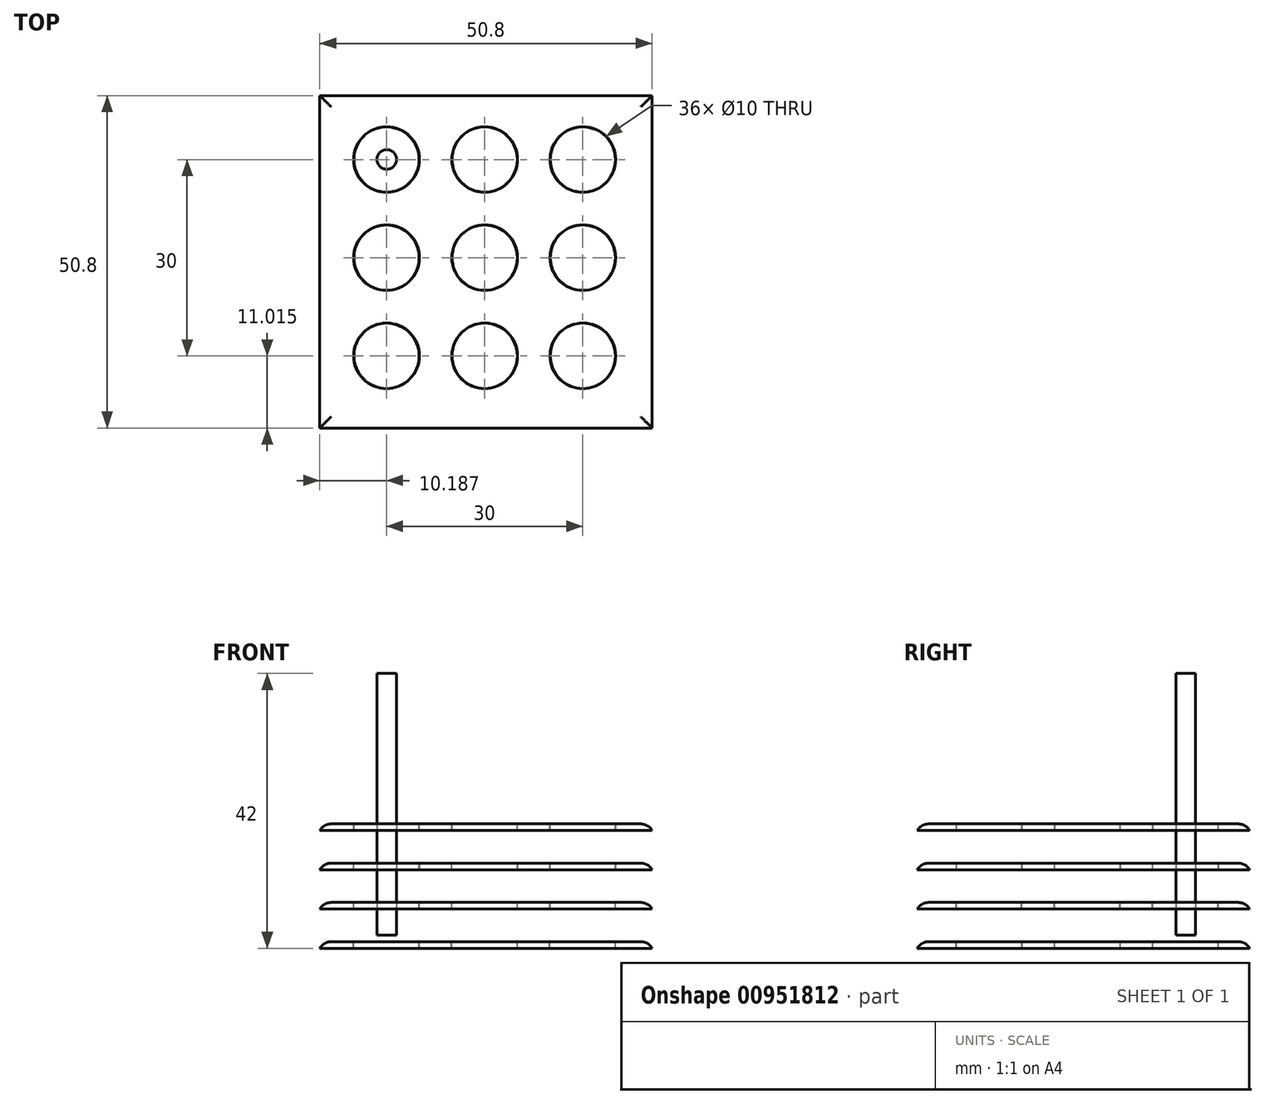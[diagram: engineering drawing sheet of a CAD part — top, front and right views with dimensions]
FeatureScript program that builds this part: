
annotation { "Feature Type Name" : "Feature", "Feature Type Description" : "" }
export const myFeature = defineFeature(function(context is Context, id is Id, definition is map)
    precondition{}
    {
        {
            var Q0;
            Q0=qCreatedBy(makeId("Top.planeOp"),FACE);
            var sketch = newSketch(context, id + "F0", { "sketchPlane" : qUnion([Q0])});
            skLineSegment(sketch, "E0.bottom", {"start": v(-21.15, 0) * mm, "end": v(29.65, 0) * mm});
            skLineSegment(sketch, "E0.top", {"start": v(-21.15, 50.8) * mm, "end": v(29.65, 50.8) * mm});
            skLineSegment(sketch, "E0.left", {"start": v(-21.15, 0) * mm, "end": v(-21.15, 50.8) * mm});
            skLineSegment(sketch, "E0.right", {"start": v(29.65, 0) * mm, "end": v(29.65, 50.8) * mm});
            skSolve(sketch);
        }
        {
            var Q0;
            Q0=makeQuery(id+"F0.imprint","IMPRINT",FACE,{"disambiguationData":[TD([[makeQuery(id+"F0.imprint","IMPRINT",EDGE,{"derivedFrom":sQuery(id+"F0.wireOp",EDGE,"E0.bottom")}),1.0]])]});
            extrude(context, id + "F1", {"entities" : qUnion([Q0]), "depth" : 1 * mm, "offsetDistance" : 25.4 * mm});
        }
        {
            var Q0;
            Q0=makeQuery(id+"F1.opExtrude","CAP_EDGE",EDGE,{"disambiguationData":[OSD([sQuery(id+"F0.wireOp",EDGE,"E0.bottom")])],"isStart":false});
            var Q1;
            Q1=makeQuery(id+"F1.opExtrude","CAP_EDGE",EDGE,{"disambiguationData":[OSD([sQuery(id+"F0.wireOp",EDGE,"E0.right")])],"isStart":false});
            var Q2;
            Q2=makeQuery(id+"F1.opExtrude","CAP_EDGE",EDGE,{"disambiguationData":[OSD([sQuery(id+"F0.wireOp",EDGE,"E0.top")])],"isStart":false});
            var Q3;
            Q3=makeQuery(id+"F1.opExtrude","CAP_EDGE",EDGE,{"disambiguationData":[OSD([sQuery(id+"F0.wireOp",EDGE,"E0.left")])],"isStart":false});
            fillet(context, id + "F2", {"entities" : qUnion([Q0, Q1, Q2, Q3]), "radius" : 2 * mm, "tangentPropagation" : true, "allowEdgeOverflow" : false});
        }
        {
            var Q0;
            Q0=makeQuery(id+"F1.opExtrude","CAP_FACE",FACE,{"disambiguationData":[OSD([sQuery(id+"F0.wireOp",EDGE,"E0.bottom"),sQuery(id+"F0.wireOp",EDGE,"E0.top"),sQuery(id+"F0.wireOp",EDGE,"E0.left"),sQuery(id+"F0.wireOp",EDGE,"E0.right")])],"isStart":false});
            var sketch = newSketch(context, id + "F3", { "sketchPlane" : qUnion([Q0])});
            skPoint(sketch, "E1", {"position": v(-10.96, 11.01) * mm});
            skPoint(sketch, "E2.0.1.0", {"position": v(-10.96, 26.01) * mm});
            skPoint(sketch, "E2.1.0.0", {"position": v(4.04, 11.01) * mm});
            skPoint(sketch, "E2.1.1.0", {"position": v(4.04, 26.01) * mm});
            skPoint(sketch, "E2.2.0.0", {"position": v(19.04, 11.01) * mm});
            skPoint(sketch, "E2.2.1.0", {"position": v(19.04, 26.01) * mm});
            skLineSegment(sketch, "E2.direction1", {"start": v(-10.96, 11.01) * mm, "end": v(4.04, 11.01) * mm, "construction": true});
            skLineSegment(sketch, "E2.direction2", {"start": v(-10.96, 11.01) * mm, "end": v(-10.96, 26.01) * mm, "construction": true});
            skPoint(sketch, "E3.0.0.2", {"position": v(-10.96, 41.01) * mm});
            skPoint(sketch, "E3.0.1.2", {"position": v(4.04, 41.01) * mm});
            skPoint(sketch, "E3.0.2.2", {"position": v(19.04, 41.01) * mm});
            skSolve(sketch);
        }
        {
            var Q0;
            Q0=sQuery(id+"F3.wireOp",VERTEX,"E3.0.2.2");
            var Q1;
            Q1=sQuery(id+"F3.wireOp",VERTEX,"E2.2.1.0");
            var Q2;
            Q2=sQuery(id+"F3.wireOp",VERTEX,"E2.2.0.0");
            var Q3;
            Q3=sQuery(id+"F3.wireOp",VERTEX,"E2.1.0.0");
            var Q4;
            Q4=sQuery(id+"F3.wireOp",VERTEX,"E2.1.1.0");
            var Q5;
            Q5=sQuery(id+"F3.wireOp",VERTEX,"E3.0.1.2");
            var Q6;
            Q6=sQuery(id+"F3.wireOp",VERTEX,"E3.0.0.2");
            var Q7;
            Q7=sQuery(id+"F3.wireOp",VERTEX,"E2.0.1.0");
            var Q8;
            Q8=sQuery(id+"F3.wireOp",VERTEX,"E1");
            var Q9;
            Q9=makeQuery(id+"F1.opExtrude","SWEPT_BODY",BODY,{"disambiguationData":[OSD([sQuery(id+"F0.wireOp",EDGE,"E0.bottom"),sQuery(id+"F0.wireOp",EDGE,"E0.top"),sQuery(id+"F0.wireOp",EDGE,"E0.left"),sQuery(id+"F0.wireOp",EDGE,"E0.right")])]});
            hole(context, id + "F4", {"style" : HoleStyle.SIMPLE, "endStyle" : HoleEndStyle.BLIND, "holeDiameter" : 10 * mm, "majorDiameter" : 5 * mm, "holeDepth" : 1 * mm, "isTappedThrough" : true, "tappedDepth" : 12 * mm, "tapClearance" : 3, "locations" : qUnion([Q0, Q1, Q2, Q3, Q4, Q5, Q6, Q7, Q8]), "scope" : qUnion([Q9])});
        }
        {
            var Q0;
            Q0=makeQuery(id+"F1.opExtrude","CAP_FACE",FACE,{"disambiguationData":[OSD([sQuery(id+"F0.wireOp",EDGE,"E0.bottom"),sQuery(id+"F0.wireOp",EDGE,"E0.top"),sQuery(id+"F0.wireOp",EDGE,"E0.left"),sQuery(id+"F0.wireOp",EDGE,"E0.right")])],"isStart":false});
            cPlane(context, id + "F5", {"entities" : qUnion([Q0]), "cplaneType" : CPlaneType.OFFSET, "offset" : 0 * mm, "width" : 150 * mm, "height" : 150 * mm});
        }
        {
            var Q0;
            Q0=qCreatedBy(id+"F5.planeOp",FACE);
            var sketch = newSketch(context, id + "F6", { "sketchPlane" : qUnion([Q0])});
            skCircle(sketch, "E4", {"center": v(-10.99, 41.02) * mm, "radius": 5.04 * mm});
            skCircle(sketch, "E5.0.1.0", {"center": v(-10.99, 26.02) * mm, "radius": 5.04 * mm});
            skCircle(sketch, "E5.0.2.0", {"center": v(-10.99, 11.02) * mm, "radius": 5.04 * mm});
            skCircle(sketch, "E5.1.0.0", {"center": v(4.01, 41.02) * mm, "radius": 5.04 * mm});
            skCircle(sketch, "E5.1.1.0", {"center": v(4.01, 26.02) * mm, "radius": 5.04 * mm});
            skCircle(sketch, "E5.1.2.0", {"center": v(4.01, 11.02) * mm, "radius": 5.04 * mm});
            skCircle(sketch, "E5.2.0.0", {"center": v(19.01, 41.02) * mm, "radius": 5.04 * mm});
            skCircle(sketch, "E5.2.1.0", {"center": v(19.01, 26.02) * mm, "radius": 5.04 * mm});
            skCircle(sketch, "E5.2.2.0", {"center": v(19.01, 11.02) * mm, "radius": 5.04 * mm});
            skLineSegment(sketch, "E5.direction1", {"start": v(-10.99, 41.02) * mm, "end": v(4.01, 41.02) * mm, "construction": true});
            skLineSegment(sketch, "E5.direction2", {"start": v(-10.99, 41.02) * mm, "end": v(-10.99, 26.02) * mm, "construction": true});
            skSolve(sketch);
        }
        {
            var Q0;
            Q0=makeQuery(id+"F6.imprint","IMPRINT",FACE,{"disambiguationData":[TD([[makeQuery(id+"F6.imprint","IMPRINT",EDGE,{"derivedFrom":sQuery(id+"F6.wireOp",EDGE,"E4")}),1.0]])]});
            var Q1;
            Q1=makeQuery(id+"F6.imprint","IMPRINT",FACE,{"disambiguationData":[TD([[makeQuery(id+"F6.imprint","IMPRINT",EDGE,{"derivedFrom":sQuery(id+"F6.wireOp",EDGE,"E5.1.0.0")}),1.0]])]});
            var Q2;
            Q2=makeQuery(id+"F6.imprint","IMPRINT",FACE,{"disambiguationData":[TD([[makeQuery(id+"F6.imprint","IMPRINT",EDGE,{"derivedFrom":sQuery(id+"F6.wireOp",EDGE,"E5.2.0.0")}),1.0]])]});
            var Q3;
            Q3=makeQuery(id+"F6.imprint","IMPRINT",FACE,{"disambiguationData":[TD([[makeQuery(id+"F6.imprint","IMPRINT",EDGE,{"derivedFrom":sQuery(id+"F6.wireOp",EDGE,"E5.0.1.0")}),1.0]])]});
            var Q4;
            Q4=makeQuery(id+"F6.imprint","IMPRINT",FACE,{"disambiguationData":[TD([[makeQuery(id+"F6.imprint","IMPRINT",EDGE,{"derivedFrom":sQuery(id+"F6.wireOp",EDGE,"E5.1.1.0")}),1.0]])]});
            var Q5;
            Q5=makeQuery(id+"F6.imprint","IMPRINT",FACE,{"disambiguationData":[TD([[makeQuery(id+"F6.imprint","IMPRINT",EDGE,{"derivedFrom":sQuery(id+"F6.wireOp",EDGE,"E5.2.1.0")}),1.0]])]});
            var Q6;
            Q6=makeQuery(id+"F6.imprint","IMPRINT",FACE,{"disambiguationData":[TD([[makeQuery(id+"F6.imprint","IMPRINT",EDGE,{"derivedFrom":sQuery(id+"F6.wireOp",EDGE,"E5.0.2.0")}),1.0]])]});
            var Q7;
            Q7=makeQuery(id+"F6.imprint","IMPRINT",FACE,{"disambiguationData":[TD([[makeQuery(id+"F6.imprint","IMPRINT",EDGE,{"derivedFrom":sQuery(id+"F6.wireOp",EDGE,"E5.1.2.0")}),1.0]])]});
            var Q8;
            Q8=makeQuery(id+"F6.imprint","IMPRINT",FACE,{"disambiguationData":[TD([[makeQuery(id+"F6.imprint","IMPRINT",EDGE,{"derivedFrom":sQuery(id+"F6.wireOp",EDGE,"E5.2.2.0")}),1.0]])]});
            extrude(context, id + "F7", {"entities" : qUnion([Q0, Q1, Q2, Q3, Q4, Q5, Q6, Q7, Q8]), "oppositeDirection" : true, "depth" : 1 * mm, "offsetDistance" : 25 * mm});
        }
        {
            var Q0;
            Q0=makeQuery(id+"F1.opExtrude","SWEPT_BODY",BODY,{"disambiguationData":[OSD([sQuery(id+"F0.wireOp",EDGE,"E0.bottom"),sQuery(id+"F0.wireOp",EDGE,"E0.top"),sQuery(id+"F0.wireOp",EDGE,"E0.left"),sQuery(id+"F0.wireOp",EDGE,"E0.right")])]});
            transform(context, id + "F8", {"entities" : qUnion([Q0]), "transformType" : TransformType.TRANSLATION_3D, "dx" : 0 * mm, "dy" : 0 * mm, "dz" : 6 * mm, "makeCopy" : true});
        }
        {
            var Q0;
            Q0=makeQuery(id+"F8.opPattern","COPY",FACE,{"derivedFrom":makeQuery(id+"F1.opExtrude","CAP_FACE",FACE,{"disambiguationData":[OSD([sQuery(id+"F0.wireOp",EDGE,"E0.bottom"),sQuery(id+"F0.wireOp",EDGE,"E0.top"),sQuery(id+"F0.wireOp",EDGE,"E0.left"),sQuery(id+"F0.wireOp",EDGE,"E0.right")])],"isStart":false}),"instanceName":"1"});
            cPlane(context, id + "F9", {"entities" : qUnion([Q0]), "cplaneType" : CPlaneType.OFFSET, "offset" : 0 * mm, "width" : 150 * mm, "height" : 150 * mm});
        }
        {
            var Q0;
            Q0=qCreatedBy(id+"F9.planeOp",FACE);
            var sketch = newSketch(context, id + "F10", { "sketchPlane" : qUnion([Q0])});
            skCircle(sketch, "E6", {"center": v(19.06, 40.94) * mm, "radius": 5 * mm});
            skPoint(sketch, "E6.first.point", {"position": v(14.07, 41.19) * mm});
            skPoint(sketch, "E6.second.point", {"position": v(20.07, 45.84) * mm});
            skPoint(sketch, "E6.third.point", {"position": v(15.36, 37.59) * mm});
            skCircle(sketch, "E7.0.1.0", {"center": v(19.06, 25.94) * mm, "radius": 5 * mm});
            skCircle(sketch, "E7.0.2.0", {"center": v(19.06, 10.94) * mm, "radius": 5 * mm});
            skCircle(sketch, "E7.1.0.0", {"center": v(4.06, 40.94) * mm, "radius": 5 * mm});
            skCircle(sketch, "E7.1.1.0", {"center": v(4.06, 25.94) * mm, "radius": 5 * mm});
            skCircle(sketch, "E7.1.2.0", {"center": v(4.06, 10.94) * mm, "radius": 5 * mm});
            skCircle(sketch, "E7.2.0.0", {"center": v(-10.94, 40.94) * mm, "radius": 5 * mm});
            skCircle(sketch, "E7.2.1.0", {"center": v(-10.94, 25.94) * mm, "radius": 5 * mm});
            skCircle(sketch, "E7.2.2.0", {"center": v(-10.94, 10.94) * mm, "radius": 5 * mm});
            skLineSegment(sketch, "E7.direction1", {"start": v(19.06, 40.94) * mm, "end": v(4.06, 40.94) * mm, "construction": true});
            skLineSegment(sketch, "E7.direction2", {"start": v(19.06, 40.94) * mm, "end": v(19.06, 25.94) * mm, "construction": true});
            skSolve(sketch);
        }
        {
            var Q0;
            Q0=makeQuery(id+"F10.imprint","IMPRINT",FACE,{"disambiguationData":[TD([[makeQuery(id+"F10.imprint","IMPRINT",EDGE,{"derivedFrom":sQuery(id+"F10.wireOp",EDGE,"E6")}),1.0]])]});
            var Q1;
            Q1=makeQuery(id+"F10.imprint","IMPRINT",FACE,{"disambiguationData":[TD([[makeQuery(id+"F10.imprint","IMPRINT",EDGE,{"derivedFrom":sQuery(id+"F10.wireOp",EDGE,"E7.0.1.0")}),1.0]])]});
            var Q2;
            Q2=makeQuery(id+"F10.imprint","IMPRINT",FACE,{"disambiguationData":[TD([[makeQuery(id+"F10.imprint","IMPRINT",EDGE,{"derivedFrom":sQuery(id+"F10.wireOp",EDGE,"E7.0.2.0")}),1.0]])]});
            var Q3;
            Q3=makeQuery(id+"F10.imprint","IMPRINT",FACE,{"disambiguationData":[TD([[makeQuery(id+"F10.imprint","IMPRINT",EDGE,{"derivedFrom":sQuery(id+"F10.wireOp",EDGE,"E7.1.0.0")}),1.0]])]});
            var Q4;
            Q4=makeQuery(id+"F10.imprint","IMPRINT",FACE,{"disambiguationData":[TD([[makeQuery(id+"F10.imprint","IMPRINT",EDGE,{"derivedFrom":sQuery(id+"F10.wireOp",EDGE,"E7.1.1.0")}),1.0]])]});
            var Q5;
            Q5=makeQuery(id+"F10.imprint","IMPRINT",FACE,{"disambiguationData":[TD([[makeQuery(id+"F10.imprint","IMPRINT",EDGE,{"derivedFrom":sQuery(id+"F10.wireOp",EDGE,"E7.1.2.0")}),1.0]])]});
            var Q6;
            Q6=makeQuery(id+"F10.imprint","IMPRINT",FACE,{"disambiguationData":[TD([[makeQuery(id+"F10.imprint","IMPRINT",EDGE,{"derivedFrom":sQuery(id+"F10.wireOp",EDGE,"E7.2.2.0")}),1.0]])]});
            var Q7;
            Q7=makeQuery(id+"F10.imprint","IMPRINT",FACE,{"disambiguationData":[TD([[makeQuery(id+"F10.imprint","IMPRINT",EDGE,{"derivedFrom":sQuery(id+"F10.wireOp",EDGE,"E7.2.1.0")}),1.0]])]});
            var Q8;
            Q8=makeQuery(id+"F10.imprint","IMPRINT",FACE,{"disambiguationData":[TD([[makeQuery(id+"F10.imprint","IMPRINT",EDGE,{"derivedFrom":sQuery(id+"F10.wireOp",EDGE,"E7.2.0.0")}),1.0]])]});
            extrude(context, id + "F11", {"entities" : qUnion([Q0, Q1, Q2, Q3, Q4, Q5, Q6, Q7, Q8]), "oppositeDirection" : true, "depth" : 1 * mm, "offsetDistance" : 25 * mm});
        }
        {
            var Q0;
            Q0=makeQuery(id+"F8.opPattern","COPY",BODY,{"derivedFrom":makeQuery(id+"F1.opExtrude","SWEPT_BODY",BODY,{"disambiguationData":[OSD([sQuery(id+"F0.wireOp",EDGE,"E0.bottom"),sQuery(id+"F0.wireOp",EDGE,"E0.top"),sQuery(id+"F0.wireOp",EDGE,"E0.left"),sQuery(id+"F0.wireOp",EDGE,"E0.right")])]}),"instanceName":"1"});
            transform(context, id + "F12", {"entities" : qUnion([Q0]), "transformType" : TransformType.TRANSLATION_3D, "dx" : 0 * mm, "dy" : 0 * mm, "dz" : 6 * mm, "makeCopy" : true});
        }
        {
            var Q0;
            Q0=makeQuery(id+"F12.opPattern","COPY",FACE,{"derivedFrom":makeQuery(id+"F8.opPattern","COPY",FACE,{"derivedFrom":makeQuery(id+"F1.opExtrude","CAP_FACE",FACE,{"disambiguationData":[OSD([sQuery(id+"F0.wireOp",EDGE,"E0.bottom"),sQuery(id+"F0.wireOp",EDGE,"E0.top"),sQuery(id+"F0.wireOp",EDGE,"E0.left"),sQuery(id+"F0.wireOp",EDGE,"E0.right")])],"isStart":false}),"instanceName":"1"}),"instanceName":"1"});
            cPlane(context, id + "F13", {"entities" : qUnion([Q0]), "cplaneType" : CPlaneType.OFFSET, "offset" : 0 * mm, "width" : 150 * mm, "height" : 150 * mm});
        }
        {
            var Q0;
            Q0=qCreatedBy(id+"F13.planeOp",FACE);
            var sketch = newSketch(context, id + "F14", { "sketchPlane" : qUnion([Q0])});
            skCircle(sketch, "E8", {"center": v(-10.9, 41.03) * mm, "radius": 5.04 * mm});
            skPoint(sketch, "E8.first.point", {"position": v(-5.86, 41.16) * mm});
            skPoint(sketch, "E8.second.point", {"position": v(-11.96, 36.1) * mm});
            skPoint(sketch, "E8.third.point", {"position": v(-15.27, 43.55) * mm});
            skCircle(sketch, "E9.0.1.0", {"center": v(-10.9, 26.03) * mm, "radius": 5.04 * mm});
            skCircle(sketch, "E9.0.2.0", {"center": v(-10.9, 11.03) * mm, "radius": 5.04 * mm});
            skCircle(sketch, "E9.1.0.0", {"center": v(4.1, 41.03) * mm, "radius": 5.04 * mm});
            skCircle(sketch, "E9.1.1.0", {"center": v(4.1, 26.03) * mm, "radius": 5.04 * mm});
            skCircle(sketch, "E9.1.2.0", {"center": v(4.1, 11.03) * mm, "radius": 5.04 * mm});
            skCircle(sketch, "E9.2.0.0", {"center": v(19.1, 41.03) * mm, "radius": 5.04 * mm});
            skCircle(sketch, "E9.2.1.0", {"center": v(19.1, 26.03) * mm, "radius": 5.04 * mm});
            skCircle(sketch, "E9.2.2.0", {"center": v(19.1, 11.03) * mm, "radius": 5.04 * mm});
            skLineSegment(sketch, "E9.direction1", {"start": v(-10.9, 41.03) * mm, "end": v(4.1, 41.03) * mm, "construction": true});
            skLineSegment(sketch, "E9.direction2", {"start": v(-10.9, 41.03) * mm, "end": v(-10.9, 26.03) * mm, "construction": true});
            skSolve(sketch);
        }
        {
            var Q0;
            Q0 = qSketchRegion(id + "F14", true);
            extrude(context, id + "F15", {"entities" : qUnion([Q0]), "oppositeDirection" : true, "depth" : 1 * mm, "offsetDistance" : 25 * mm});
        }
        {
            var Q0;
            Q0=makeQuery(id+"F12.opPattern","COPY",BODY,{"derivedFrom":makeQuery(id+"F8.opPattern","COPY",BODY,{"derivedFrom":makeQuery(id+"F1.opExtrude","SWEPT_BODY",BODY,{"disambiguationData":[OSD([sQuery(id+"F0.wireOp",EDGE,"E0.bottom"),sQuery(id+"F0.wireOp",EDGE,"E0.top"),sQuery(id+"F0.wireOp",EDGE,"E0.left"),sQuery(id+"F0.wireOp",EDGE,"E0.right")])]}),"instanceName":"1"}),"instanceName":"1"});
            transform(context, id + "F16", {"entities" : qUnion([Q0]), "transformType" : TransformType.TRANSLATION_3D, "dx" : 0 * mm, "dy" : 0 * mm, "dz" : 6 * mm, "makeCopy" : true});
        }
        {
            var Q0;
            Q0=makeQuery(id+"F16.opPattern","COPY",FACE,{"derivedFrom":makeQuery(id+"F12.opPattern","COPY",FACE,{"derivedFrom":makeQuery(id+"F8.opPattern","COPY",FACE,{"derivedFrom":makeQuery(id+"F1.opExtrude","CAP_FACE",FACE,{"disambiguationData":[OSD([sQuery(id+"F0.wireOp",EDGE,"E0.bottom"),sQuery(id+"F0.wireOp",EDGE,"E0.top"),sQuery(id+"F0.wireOp",EDGE,"E0.left"),sQuery(id+"F0.wireOp",EDGE,"E0.right")])],"isStart":false}),"instanceName":"1"}),"instanceName":"1"}),"instanceName":"1"});
            cPlane(context, id + "F17", {"entities" : qUnion([Q0]), "cplaneType" : CPlaneType.OFFSET, "offset" : 0 * mm, "width" : 150 * mm, "height" : 150 * mm});
        }
        {
            var Q0;
            Q0=qCreatedBy(id+"F17.planeOp",FACE);
            var sketch = newSketch(context, id + "F18", { "sketchPlane" : qUnion([Q0])});
            skCircle(sketch, "E10", {"center": v(-10.9, 41.04) * mm, "radius": 5 * mm});
            skPoint(sketch, "E10.first.point", {"position": v(-5.9, 40.83) * mm});
            skPoint(sketch, "E10.second.point", {"position": v(-13.4, 36.7) * mm});
            skPoint(sketch, "E10.third.point", {"position": v(-13.54, 45.3) * mm});
            skCircle(sketch, "E11.0.1.0", {"center": v(-10.9, 26.04) * mm, "radius": 5 * mm});
            skCircle(sketch, "E11.0.2.0", {"center": v(-10.9, 11.04) * mm, "radius": 5 * mm});
            skCircle(sketch, "E11.1.0.0", {"center": v(4.1, 41.04) * mm, "radius": 5 * mm});
            skCircle(sketch, "E11.1.1.0", {"center": v(4.1, 26.04) * mm, "radius": 5 * mm});
            skCircle(sketch, "E11.1.2.0", {"center": v(4.1, 11.04) * mm, "radius": 5 * mm});
            skCircle(sketch, "E11.2.0.0", {"center": v(19.1, 41.04) * mm, "radius": 5 * mm});
            skCircle(sketch, "E11.2.1.0", {"center": v(19.1, 26.04) * mm, "radius": 5 * mm});
            skCircle(sketch, "E11.2.2.0", {"center": v(19.1, 11.04) * mm, "radius": 5 * mm});
            skLineSegment(sketch, "E11.direction1", {"start": v(-10.9, 41.04) * mm, "end": v(4.1, 41.04) * mm, "construction": true});
            skLineSegment(sketch, "E11.direction2", {"start": v(-10.9, 41.04) * mm, "end": v(-10.9, 26.04) * mm, "construction": true});
            skSolve(sketch);
        }
        {
            var Q0;
            Q0 = qSketchRegion(id + "F18", true);
            extrude(context, id + "F19", {"entities" : qUnion([Q0]), "oppositeDirection" : true, "depth" : 1 * mm, "offsetDistance" : 25 * mm});
        }
        {
            var Q0;
            Q0=qCreatedBy(id+"F17.planeOp",FACE);
            var sketch = newSketch(context, id + "F20", { "sketchPlane" : qUnion([Q0])});
            skCircle(sketch, "E12", {"center": v(-10.9, 41.04) * mm, "radius": 1.5 * mm});
            skPoint(sketch, "E12.first.point", {"position": v(-9.4, 40.95) * mm});
            skPoint(sketch, "E12.second.point", {"position": v(-12.32, 41.56) * mm});
            skPoint(sketch, "E12.third.point", {"position": v(-10.83, 39.54) * mm});
            skSolve(sketch);
        }
        {
            var Q0;
            Q0=makeQuery(id+"F20.imprint","IMPRINT",FACE,{"disambiguationData":[TD([[makeQuery(id+"F20.imprint","IMPRINT",EDGE,{"derivedFrom":sQuery(id+"F20.wireOp",EDGE,"E12")}),1.0]])]});
            extrude(context, id + "F21", {"entities" : qUnion([Q0]), "depth" : 40 * mm, "offsetDistance" : 25 * mm});
        }
        {
            var Q0;
            Q0=makeQuery(id+"F21.opExtrude","SWEPT_BODY",BODY,{"disambiguationData":[OSD([sQuery(id+"F20.wireOp",EDGE,"E12")])]});
            transform(context, id + "F22", {"entities" : qUnion([Q0]), "transformType" : TransformType.TRANSLATION_3D, "dx" : 0 * mm, "dy" : 0 * mm, "dz" : -17 * mm, "makeCopy" : false});
        }
    });
